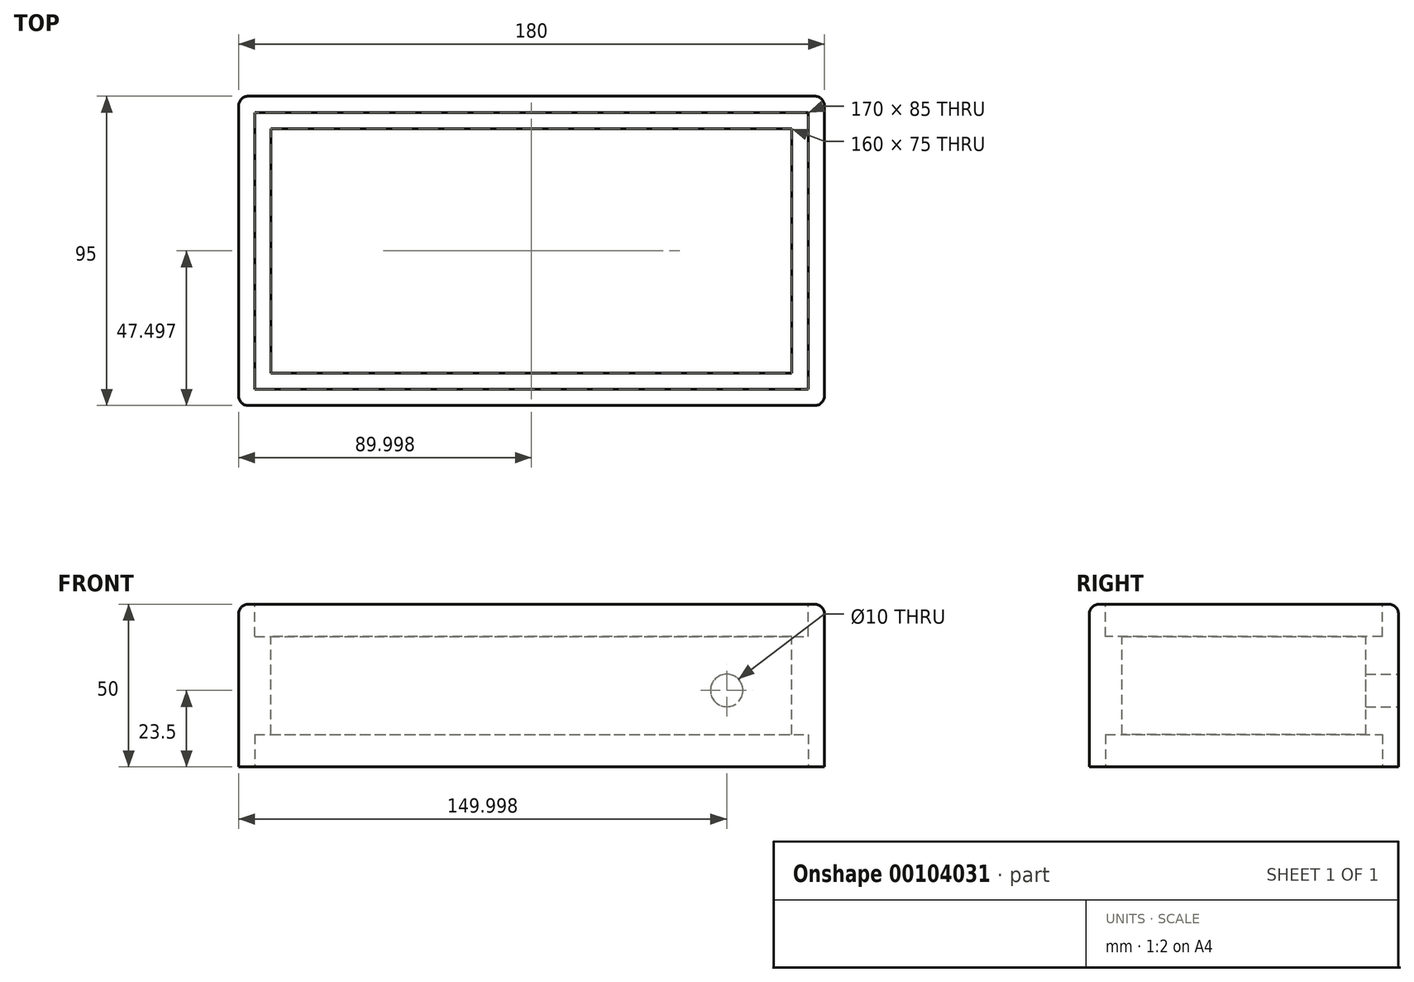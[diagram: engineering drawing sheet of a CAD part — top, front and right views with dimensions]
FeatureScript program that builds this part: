
annotation { "Feature Type Name" : "Feature", "Feature Type Description" : "" }
export const myFeature = defineFeature(function(context is Context, id is Id, definition is map)
    precondition{}
    {
        {
            var Q0;
            Q0=qCreatedBy(makeId("Top.planeOp"),FACE);
            var sketch = newSketch(context, id + "F0", { "sketchPlane" : qUnion([Q0])});
            skLineSegment(sketch, "E0.bottom", {"start": v(-92.01, 36.14) * mm, "end": v(87.99, 36.14) * mm});
            skLineSegment(sketch, "E0.top", {"start": v(-92.01, -58.86) * mm, "end": v(87.99, -58.86) * mm});
            skLineSegment(sketch, "E0.left", {"start": v(-92.01, 36.14) * mm, "end": v(-92.01, -58.86) * mm});
            skLineSegment(sketch, "E0.right", {"start": v(87.99, 36.14) * mm, "end": v(87.99, -58.86) * mm});
            skSolve(sketch);
        }
        {
            var Q0;
            Q0 = qSketchRegion(id + "F0", true);
            extrude(context, id + "F1", {"entities" : qUnion([Q0]), "depth" : 50 * mm, "offsetDistance" : 25 * mm});
        }
        {
            var Q0;
            Q0=makeQuery(id+"F1.opExtrude","CAP_FACE",FACE,{"disambiguationData":[OSD([sQuery(id+"F0.wireOp",EDGE,"E0.bottom"),sQuery(id+"F0.wireOp",EDGE,"E0.top"),sQuery(id+"F0.wireOp",EDGE,"E0.left"),sQuery(id+"F0.wireOp",EDGE,"E0.right")])],"isStart":false});
            var sketch = newSketch(context, id + "F2", { "sketchPlane" : qUnion([Q0])});
            skLineSegment(sketch, "E1.bottom", {"start": v(-82.01, 26.14) * mm, "end": v(77.99, 26.14) * mm});
            skLineSegment(sketch, "E1.top", {"start": v(-82.01, -48.86) * mm, "end": v(77.99, -48.86) * mm});
            skLineSegment(sketch, "E1.left", {"start": v(-82.01, 26.14) * mm, "end": v(-82.01, -48.86) * mm});
            skLineSegment(sketch, "E1.right", {"start": v(77.99, 26.14) * mm, "end": v(77.99, -48.86) * mm});
            skSolve(sketch);
        }
        {
            var Q0;
            Q0 = qSketchRegion(id + "F2", true);
            extrude(context, id + "F3", {"entities" : qUnion([Q0]), "operationType" : NewBodyOperationType.REMOVE, "endBound" : BoundingType.THROUGH_ALL, "oppositeDirection" : true, "depth" : 25 * mm, "offsetDistance" : 25 * mm});
        }
        {
            var Q0;
            Q0=makeQuery(id+"F1.opExtrude","CAP_FACE",FACE,{"disambiguationData":[OSD([sQuery(id+"F0.wireOp",EDGE,"E0.bottom"),sQuery(id+"F0.wireOp",EDGE,"E0.top"),sQuery(id+"F0.wireOp",EDGE,"E0.left"),sQuery(id+"F0.wireOp",EDGE,"E0.right")])],"isStart":false});
            var sketch = newSketch(context, id + "F4", { "sketchPlane" : qUnion([Q0])});
            skLineSegment(sketch, "E2.bottom", {"start": v(-87.01, 31.14) * mm, "end": v(82.99, 31.14) * mm});
            skLineSegment(sketch, "E2.top", {"start": v(-87.01, -53.86) * mm, "end": v(82.99, -53.86) * mm});
            skLineSegment(sketch, "E2.left", {"start": v(-87.01, 31.14) * mm, "end": v(-87.01, -53.86) * mm});
            skLineSegment(sketch, "E2.right", {"start": v(82.99, 31.14) * mm, "end": v(82.99, -53.86) * mm});
            skSolve(sketch);
        }
        {
            var Q0;
            Q0 = qSketchRegion(id + "F4", true);
            extrude(context, id + "F5", {"entities" : qUnion([Q0]), "operationType" : NewBodyOperationType.REMOVE, "oppositeDirection" : true, "depth" : 10 * mm, "offsetDistance" : 25 * mm});
        }
        {
            var Q0;
            Q0=makeQuery(id+"F1.opExtrude","CAP_FACE",FACE,{"disambiguationData":[OSD([sQuery(id+"F0.wireOp",EDGE,"E0.bottom"),sQuery(id+"F0.wireOp",EDGE,"E0.top"),sQuery(id+"F0.wireOp",EDGE,"E0.left"),sQuery(id+"F0.wireOp",EDGE,"E0.right")])],"isStart":true});
            var sketch = newSketch(context, id + "F6", { "sketchPlane" : qUnion([Q0])});
            skLineSegment(sketch, "E3.bottom", {"start": v(-87.01, 53.86) * mm, "end": v(82.99, 53.86) * mm});
            skLineSegment(sketch, "E3.top", {"start": v(-87.01, -31.14) * mm, "end": v(82.99, -31.14) * mm});
            skLineSegment(sketch, "E3.left", {"start": v(-87.01, 53.86) * mm, "end": v(-87.01, -31.14) * mm});
            skLineSegment(sketch, "E3.right", {"start": v(82.99, 53.86) * mm, "end": v(82.99, -31.14) * mm});
            skSolve(sketch);
        }
        {
            var Q0;
            Q0 = qSketchRegion(id + "F6", true);
            extrude(context, id + "F7", {"entities" : qUnion([Q0]), "operationType" : NewBodyOperationType.REMOVE, "oppositeDirection" : true, "depth" : 10 * mm, "offsetDistance" : 25 * mm});
        }
        {
            var Q0;
            Q0=makeQuery(id+"F1.opExtrude","SWEPT_EDGE",EDGE,{"disambiguationData":[OSD([sQuery(id+"F0.wireOp",EDGE,"E0.top"),sQuery(id+"F0.wireOp",EDGE,"E0.left")])]});
            var Q1;
            Q1=makeQuery(id+"F1.opExtrude","SWEPT_EDGE",EDGE,{"disambiguationData":[OSD([sQuery(id+"F0.wireOp",EDGE,"E0.top"),sQuery(id+"F0.wireOp",EDGE,"E0.right")])]});
            var Q2;
            Q2=makeQuery(id+"F1.opExtrude","CAP_EDGE",EDGE,{"disambiguationData":[OSD([sQuery(id+"F0.wireOp",EDGE,"E0.right")])],"isStart":false});
            var Q3;
            Q3=makeQuery(id+"F1.opExtrude","CAP_EDGE",EDGE,{"disambiguationData":[OSD([sQuery(id+"F0.wireOp",EDGE,"E0.top")])],"isStart":false});
            var Q4;
            Q4=makeQuery(id+"F1.opExtrude","CAP_EDGE",EDGE,{"disambiguationData":[OSD([sQuery(id+"F0.wireOp",EDGE,"E0.left")])],"isStart":false});
            var Q5;
            Q5=makeQuery(id+"F1.opExtrude","CAP_EDGE",EDGE,{"disambiguationData":[OSD([sQuery(id+"F0.wireOp",EDGE,"E0.bottom")])],"isStart":false});
            var Q6;
            Q6=makeQuery(id+"F1.opExtrude","SWEPT_EDGE",EDGE,{"disambiguationData":[OSD([sQuery(id+"F0.wireOp",EDGE,"E0.bottom"),sQuery(id+"F0.wireOp",EDGE,"E0.left")])]});
            var Q7;
            Q7=makeQuery(id+"F1.opExtrude","SWEPT_EDGE",EDGE,{"disambiguationData":[OSD([sQuery(id+"F0.wireOp",EDGE,"E0.bottom"),sQuery(id+"F0.wireOp",EDGE,"E0.right")])]});
            fillet(context, id + "F8", {"entities" : qUnion([Q0, Q1, Q2, Q3, Q4, Q5, Q6, Q7]), "tangentPropagation" : true, "radius" : 3 * mm, "defaultsChanged" : false, "vertexSettings" : [], "allowEdgeOverflow" : false});
        }
        {
            var Q0;
            Q0=makeQuery(id+"F1.opExtrude","SWEPT_FACE",FACE,{"disambiguationData":[OSD([sQuery(id+"F0.wireOp",EDGE,"E0.bottom")])]});
            var sketch = newSketch(context, id + "F9", { "sketchPlane" : qUnion([Q0])});
            skCircle(sketch, "E4", {"center": v(-57.99, 23.5) * mm, "radius": 5 * mm});
            skPoint(sketch, "E4.centerSnap0", {"position": v(-84.99, 23.5) * mm});
            skSolve(sketch);
        }
        {
            var Q0;
            Q0 = qSketchRegion(id + "F9", true);
            extrude(context, id + "F10", {"entities" : qUnion([Q0]), "operationType" : NewBodyOperationType.REMOVE, "endBound" : BoundingType.UP_TO_NEXT, "oppositeDirection" : true, "depth" : 25 * mm, "offsetDistance" : 25 * mm});
        }
    });
